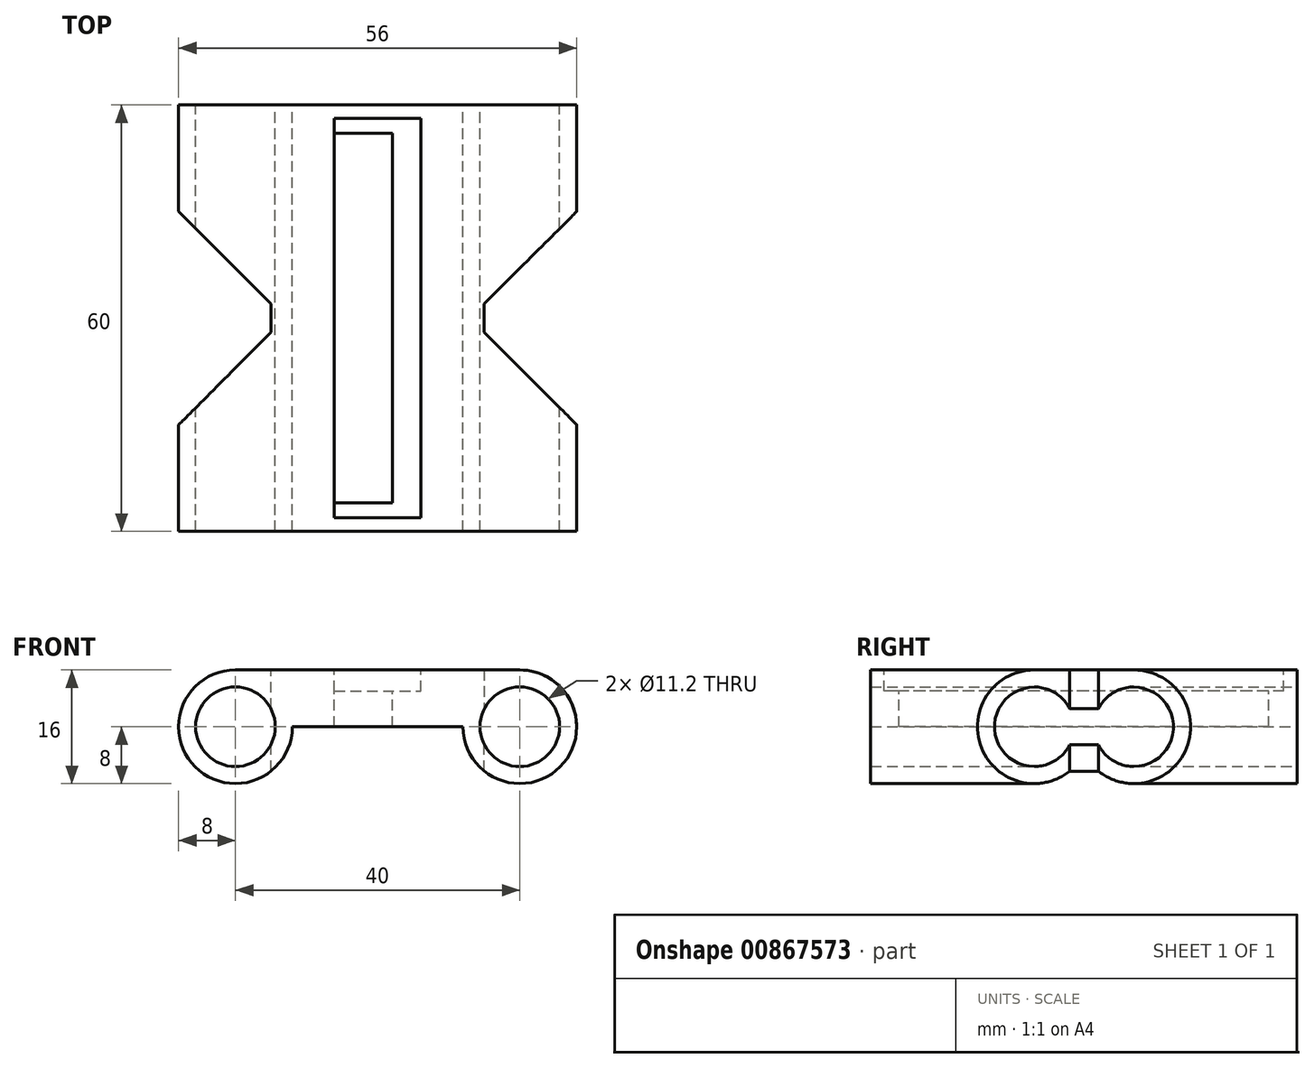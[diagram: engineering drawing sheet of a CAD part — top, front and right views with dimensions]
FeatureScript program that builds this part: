
annotation { "Feature Type Name" : "Feature", "Feature Type Description" : "" }
export const myFeature = defineFeature(function(context is Context, id is Id, definition is map)
    precondition{}
    {
        {
            var Q0;
            Q0=qCreatedBy(makeId("Front.planeOp"),FACE);
            var sketch = newSketch(context, id + "F0", { "sketchPlane" : qUnion([Q0])});
            skPoint(sketch, "E0", {"position": v(0, 0) * mm});
            skPoint(sketch, "E1", {"position": v(40, 0) * mm});
            skCircle(sketch, "E2", {"center": v(0, 0) * mm, "radius": 5.6 * mm});
            skCircle(sketch, "E3", {"center": v(40, 0) * mm, "radius": 5.6 * mm});
            skCircle(sketch, "E4", {"center": v(0, 0) * mm, "radius": 8 * mm});
            skCircle(sketch, "E5", {"center": v(40, 0) * mm, "radius": 8 * mm});
            skLineSegment(sketch, "E6", {"start": v(0, 8) * mm, "end": v(40, 8) * mm});
            skLineSegment(sketch, "E7", {"start": v(8, 0) * mm, "end": v(32, 0) * mm});
            skSolve(sketch);
        }
        {
            var Q0;
            {var subQ0=sQuery(id+"F0.wireOp",EDGE,"E6");Q0=makeQuery(id+"F0.imprint","IMPRINT",FACE,{"disambiguationData":[TD([[makeQuery(id+"F0.imprint","IMPRINT",EDGE,{"derivedFrom":subQ0}),-1.0]])]});}
            var Q1;
            Q1=makeQuery(id+"F0.imprint","IMPRINT",FACE,{"disambiguationData":[TD([[makeQuery(id+"F0.imprint","IMPRINT",EDGE,{"derivedFrom":sQuery(id+"F0.wireOp",EDGE,"E2")}),-1.0]])]});
            var Q2;
            Q2=makeQuery(id+"F0.imprint","IMPRINT",FACE,{"disambiguationData":[TD([[makeQuery(id+"F0.imprint","IMPRINT",EDGE,{"derivedFrom":sQuery(id+"F0.wireOp",EDGE,"E3")}),-1.0]])]});
            extrude(context, id + "F1", {"entities" : qUnion([Q0, Q1, Q2]), "depth" : 60 * mm, "offsetDistance" : 25 * mm});
        }
        {
            var Q0;
            Q0=makeQuery(id+"F1.opExtrude","SWEPT_FACE",FACE,{"disambiguationData":[OSD([sQuery(id+"F0.wireOp",EDGE,"E6")])]});
            var sketch = newSketch(context, id + "F2", { "sketchPlane" : qUnion([Q0])});
            skLineSegment(sketch, "E8.bottom", {"start": v(13.9, -1.9) * mm, "end": v(26.1, -1.9) * mm});
            skLineSegment(sketch, "E8.top", {"start": v(13.9, -58.1) * mm, "end": v(26.1, -58.1) * mm});
            skLineSegment(sketch, "E8.left", {"start": v(13.9, -1.9) * mm, "end": v(13.9, -58.1) * mm});
            skLineSegment(sketch, "E8.right", {"start": v(26.1, -1.9) * mm, "end": v(26.1, -58.1) * mm});
            skSolve(sketch);
        }
        {
            var Q0;
            Q0=makeQuery(id+"F2.imprint","IMPRINT",FACE,{"disambiguationData":[TD([[makeQuery(id+"F2.imprint","IMPRINT",EDGE,{"derivedFrom":sQuery(id+"F2.wireOp",EDGE,"E8.bottom")}),-1.0]])]});
            extrude(context, id + "F3", {"entities" : qUnion([Q0]), "operationType" : NewBodyOperationType.REMOVE, "oppositeDirection" : true, "depth" : 3 * mm, "offsetDistance" : 25 * mm});
        }
        {
            var Q0;
            Q0=makeQuery(id+"F3.boolean.opBoolean","COPY",FACE,{"derivedFrom":makeQuery(id+"F3.opExtrude","CAP_FACE",FACE,{"disambiguationData":[OSD([sQuery(id+"F2.wireOp",EDGE,"E8.bottom"),sQuery(id+"F2.wireOp",EDGE,"E8.top"),sQuery(id+"F2.wireOp",EDGE,"E8.left"),sQuery(id+"F2.wireOp",EDGE,"E8.right")])],"isStart":false})});
            var sketch = newSketch(context, id + "F4", { "sketchPlane" : qUnion([Q0])});
            skLineSegment(sketch, "E9.bottom", {"start": v(13.9, -4) * mm, "end": v(22.1, -4) * mm});
            skLineSegment(sketch, "E9.top", {"start": v(13.9, -56) * mm, "end": v(22.1, -56) * mm});
            skLineSegment(sketch, "E9.left", {"start": v(13.9, -4) * mm, "end": v(13.9, -56) * mm});
            skLineSegment(sketch, "E9.right", {"start": v(22.1, -4) * mm, "end": v(22.1, -56) * mm});
            skSolve(sketch);
        }
        {
            var Q0;
            Q0=makeQuery(id+"F4.imprint","IMPRINT",FACE,{"disambiguationData":[TD([[makeQuery(id+"F4.imprint","IMPRINT",EDGE,{"derivedFrom":sQuery(id+"F4.wireOp",EDGE,"E9.bottom")}),-1.0]])]});
            extrude(context, id + "F5", {"entities" : qUnion([Q0]), "operationType" : NewBodyOperationType.REMOVE, "oppositeDirection" : true, "depth" : 25 * mm, "offsetDistance" : 25 * mm});
        }
        {
            var Q0;
            Q0=makeQuery(id+"F1.opExtrude","SWEPT_FACE",FACE,{"disambiguationData":[OSD([sQuery(id+"F0.wireOp",EDGE,"E6")])]});
            var sketch = newSketch(context, id + "F6", { "sketchPlane" : qUnion([Q0])});
            skLineSegment(sketch, "E10", {"start": v(40, -60) * mm, "end": v(40, -45) * mm});
            skLineSegment(sketch, "E11", {"start": v(40, 0) * mm, "end": v(40, -15) * mm});
            skLineSegment(sketch, "E12", {"start": v(0, 0) * mm, "end": v(0, -15) * mm});
            skLineSegment(sketch, "E13", {"start": v(0, -60) * mm, "end": v(0, -45) * mm});
            skLineSegment(sketch, "E14", {"start": v(0, -15) * mm, "end": v(5, -15) * mm});
            skLineSegment(sketch, "E15", {"start": v(5, -15) * mm, "end": v(5, -45) * mm});
            skLineSegment(sketch, "E16", {"start": v(5, -45) * mm, "end": v(0, -45) * mm});
            skLineSegment(sketch, "E17", {"start": v(40, -15) * mm, "end": v(35, -15) * mm});
            skLineSegment(sketch, "E18", {"start": v(35, -15) * mm, "end": v(35, -45) * mm});
            skLineSegment(sketch, "E19", {"start": v(35, -45) * mm, "end": v(40, -45) * mm});
            skLineSegment(sketch, "E20", {"start": v(40, -15) * mm, "end": v(52.9, -15) * mm});
            skLineSegment(sketch, "E21", {"start": v(52.9, -15) * mm, "end": v(52.9, -45) * mm});
            skLineSegment(sketch, "E22", {"start": v(52.9, -45) * mm, "end": v(40, -45) * mm});
            skLineSegment(sketch, "E23", {"start": v(0, -15) * mm, "end": v(-17.46, -15) * mm});
            skLineSegment(sketch, "E24", {"start": v(-17.46, -15) * mm, "end": v(-17.46, -45) * mm});
            skLineSegment(sketch, "E25", {"start": v(-17.46, -45) * mm, "end": v(0, -45) * mm});
            skSolve(sketch);
        }
        {
            var Q0;
            {var subQ0=sQuery(id+"F6.wireOp",EDGE,"E23");Q0=makeQuery(id+"F6.imprint","IMPRINT",FACE,{"disambiguationData":[TD([[makeQuery(id+"F6.imprint","IMPRINT",EDGE,{"derivedFrom":subQ0}),1.0]])]});}
            var Q1;
            {var subQ0=sQuery(id+"F6.wireOp",EDGE,"E14");Q1=makeQuery(id+"F6.imprint","IMPRINT",FACE,{"disambiguationData":[TD([[makeQuery(id+"F6.imprint","IMPRINT",EDGE,{"derivedFrom":subQ0}),-1.0]])]});}
            var Q2;
            {var subQ0=sQuery(id+"F6.wireOp",EDGE,"E17");Q2=makeQuery(id+"F6.imprint","IMPRINT",FACE,{"disambiguationData":[TD([[makeQuery(id+"F6.imprint","IMPRINT",EDGE,{"derivedFrom":subQ0}),1.0]])]});}
            var Q3;
            {var subQ0=sQuery(id+"F6.wireOp",EDGE,"E20");Q3=makeQuery(id+"F6.imprint","IMPRINT",FACE,{"disambiguationData":[TD([[makeQuery(id+"F6.imprint","IMPRINT",EDGE,{"derivedFrom":subQ0}),-1.0]])]});}
            extrude(context, id + "F7", {"entities" : qUnion([Q0, Q1, Q2, Q3]), "operationType" : NewBodyOperationType.REMOVE, "oppositeDirection" : true, "depth" : 25 * mm, "offsetDistance" : 25 * mm});
        }
        {
            var Q0;
            {var subQ0=sQuery(id+"F6.wireOp",EDGE,"E15");var subQ1=sQuery(id+"F6.wireOp",EDGE,"E14");Q0=makeQuery(id+"F7.boolean.opBoolean","COPY",EDGE,{"disambiguationData":[TD([makeQuery(id+"F1.opExtrude","SWEPT_FACE",FACE,{"disambiguationData":[OSD([sQuery(id+"F0.wireOp",EDGE,"E6")])]})])],"derivedFrom":makeQuery(id+"F7.opExtrude","SWEPT_EDGE",EDGE,{"disambiguationData":[OSD([subQ1,subQ0])]})});}
            var Q1;
            {var subQ0=sQuery(id+"F6.wireOp",EDGE,"E15");var subQ1=sQuery(id+"F6.wireOp",EDGE,"E14");Q1=makeQuery(id+"F7.boolean.opBoolean","COPY",EDGE,{"disambiguationData":[TD([makeQuery(id+"F1.opExtrude","SWEPT_FACE",FACE,{"disambiguationData":[OSD([sQuery(id+"F0.wireOp",EDGE,"E4")])]})])],"derivedFrom":makeQuery(id+"F7.opExtrude","SWEPT_EDGE",EDGE,{"disambiguationData":[OSD([subQ1,subQ0])]})});}
            chamfer(context, id + "F8", {"entities" : qUnion([Q0, Q1]), "width" : 13 * mm, "tangentPropagation" : true});
        }
        {
            var Q0;
            {var subQ0=sQuery(id+"F6.wireOp",EDGE,"E15");var subQ1=sQuery(id+"F6.wireOp",EDGE,"E16");Q0=makeQuery(id+"F7.boolean.opBoolean","COPY",EDGE,{"disambiguationData":[TD([makeQuery(id+"F1.opExtrude","SWEPT_FACE",FACE,{"disambiguationData":[OSD([sQuery(id+"F0.wireOp",EDGE,"E6")])]})])],"derivedFrom":makeQuery(id+"F7.opExtrude","SWEPT_EDGE",EDGE,{"disambiguationData":[OSD([subQ0,subQ1])]})});}
            var Q1;
            {var subQ0=sQuery(id+"F6.wireOp",EDGE,"E15");var subQ1=sQuery(id+"F6.wireOp",EDGE,"E16");Q1=makeQuery(id+"F7.boolean.opBoolean","COPY",EDGE,{"disambiguationData":[TD([makeQuery(id+"F1.opExtrude","SWEPT_FACE",FACE,{"disambiguationData":[OSD([sQuery(id+"F0.wireOp",EDGE,"E4")])]})])],"derivedFrom":makeQuery(id+"F7.opExtrude","SWEPT_EDGE",EDGE,{"disambiguationData":[OSD([subQ0,subQ1])]})});}
            var Q2;
            {var subQ0=sQuery(id+"F6.wireOp",EDGE,"E17");var subQ1=sQuery(id+"F6.wireOp",EDGE,"E18");Q2=makeQuery(id+"F7.boolean.opBoolean","COPY",EDGE,{"disambiguationData":[TD([makeQuery(id+"F1.opExtrude","SWEPT_FACE",FACE,{"disambiguationData":[OSD([sQuery(id+"F0.wireOp",EDGE,"E6")])]})])],"derivedFrom":makeQuery(id+"F7.opExtrude","SWEPT_EDGE",EDGE,{"disambiguationData":[OSD([subQ0,subQ1])]})});}
            var Q3;
            {var subQ0=sQuery(id+"F6.wireOp",EDGE,"E18");var subQ1=sQuery(id+"F6.wireOp",EDGE,"E17");Q3=makeQuery(id+"F7.boolean.opBoolean","COPY",EDGE,{"disambiguationData":[TD([makeQuery(id+"F1.opExtrude","SWEPT_FACE",FACE,{"disambiguationData":[OSD([sQuery(id+"F0.wireOp",EDGE,"E5")])]})])],"derivedFrom":makeQuery(id+"F7.opExtrude","SWEPT_EDGE",EDGE,{"disambiguationData":[OSD([subQ1,subQ0])]})});}
            var Q4;
            {var subQ0=sQuery(id+"F6.wireOp",EDGE,"E19");var subQ1=sQuery(id+"F6.wireOp",EDGE,"E18");Q4=makeQuery(id+"F7.boolean.opBoolean","COPY",EDGE,{"disambiguationData":[TD([makeQuery(id+"F1.opExtrude","SWEPT_FACE",FACE,{"disambiguationData":[OSD([sQuery(id+"F0.wireOp",EDGE,"E6")])]})])],"derivedFrom":makeQuery(id+"F7.opExtrude","SWEPT_EDGE",EDGE,{"disambiguationData":[OSD([subQ1,subQ0])]})});}
            var Q5;
            {var subQ0=sQuery(id+"F6.wireOp",EDGE,"E18");var subQ1=sQuery(id+"F6.wireOp",EDGE,"E19");Q5=makeQuery(id+"F7.boolean.opBoolean","COPY",EDGE,{"disambiguationData":[TD([makeQuery(id+"F1.opExtrude","SWEPT_FACE",FACE,{"disambiguationData":[OSD([sQuery(id+"F0.wireOp",EDGE,"E5")])]})])],"derivedFrom":makeQuery(id+"F7.opExtrude","SWEPT_EDGE",EDGE,{"disambiguationData":[OSD([subQ0,subQ1])]})});}
            chamfer(context, id + "F9", {"entities" : qUnion([Q0, Q1, Q2, Q3, Q4, Q5]), "width" : 13 * mm, "tangentPropagation" : true});
        }
    });
